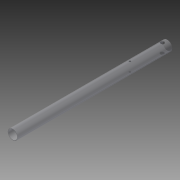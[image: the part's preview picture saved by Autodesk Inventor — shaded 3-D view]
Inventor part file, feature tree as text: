
AUTODESK INVENTOR PART (.ipt)
format: ipt  version: 2014 SP1 (Build 180222100, 222)  size: 100,864 bytes
history: native  units: in
note: dims shown in document units (in); Inventor stores cm internally (conversion verified against a paired STEP export)
features: extrude x2, sketch x2, plane x1
ambient origin geometry x8: Origin, YZ Plane, XZ Plane, XY Plane, X Axis, Y Axis, Z Axis, Center Point
bodies: Solid1 (feature_tree)
feature tree (5):
  extrude  "Extrusion1"  Depth=0.875in
  plane  "Work Plane1"
  extrude  "Extrusion2"  Depth=0.375in
  sketch  "Sketch1"  dims[d0=1.0in d1=0.875in]
  sketch  "Sketch2"  dims[d2=15.5in d3=0.0in d4=0.375in d6=0.5in d8=1.0in d9=0.0in d10=0.19in d11=3.75in]
